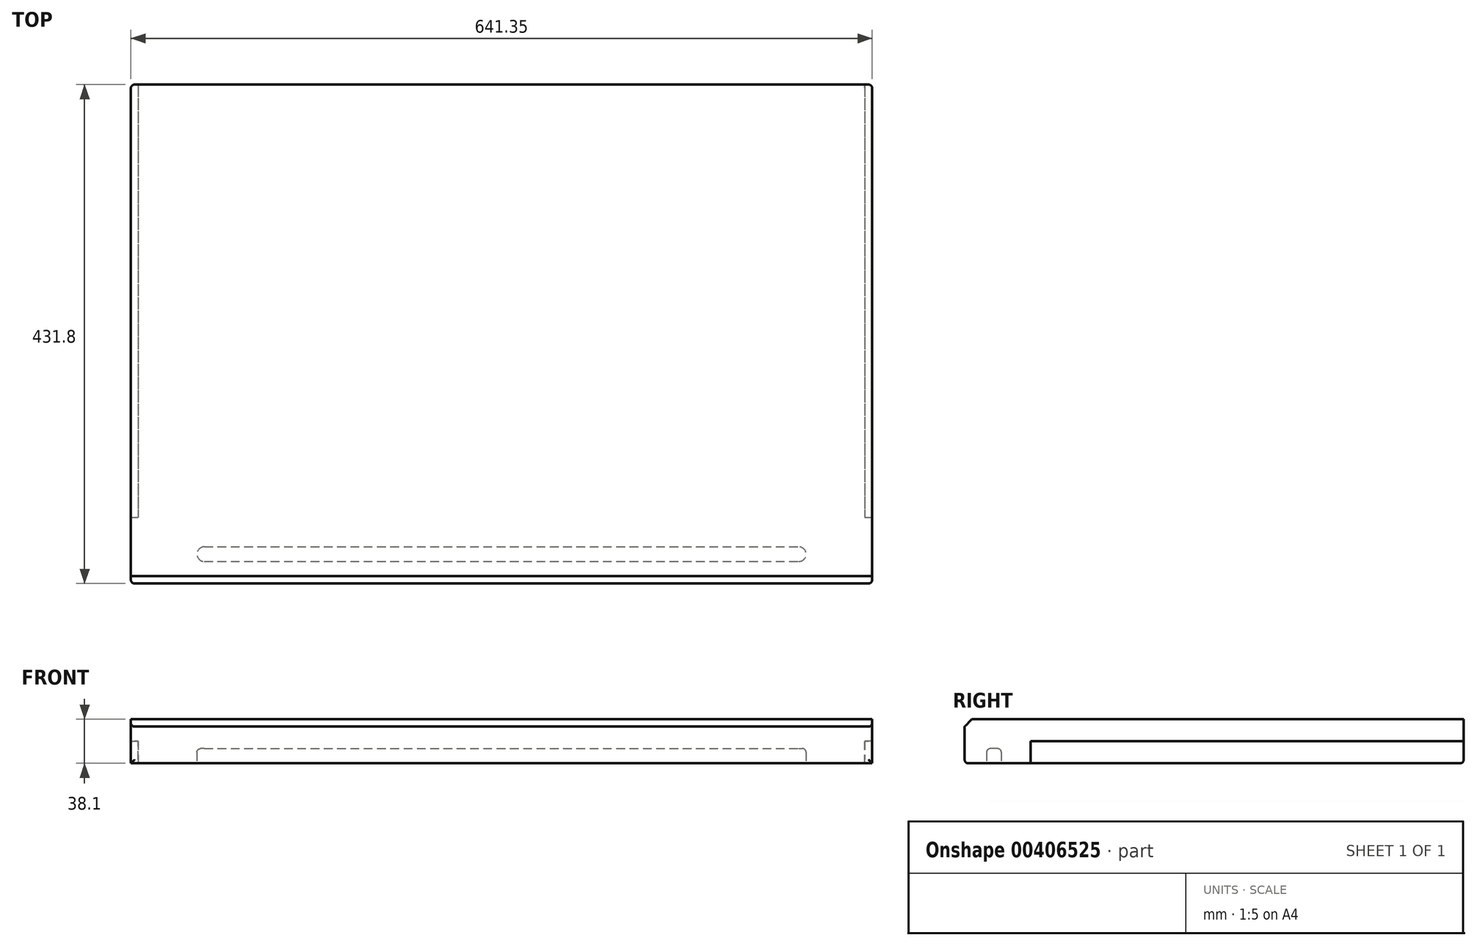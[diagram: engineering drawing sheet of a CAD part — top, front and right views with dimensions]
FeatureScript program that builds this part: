
annotation { "Feature Type Name" : "Feature", "Feature Type Description" : "" }
export const myFeature = defineFeature(function(context is Context, id is Id, definition is map)
    precondition{}
    {
        {
            var Q0;
            Q0=qCreatedBy(makeId("Top.planeOp"),FACE);
            var sketch = newSketch(context, id + "F0", { "sketchPlane" : qUnion([Q0])});
            skLineSegment(sketch, "E0.bottom", {"start": v(0, 0) * mm, "end": v(641.35, 0) * mm});
            skLineSegment(sketch, "E0.top", {"start": v(0, 431.8) * mm, "end": v(641.35, 431.8) * mm});
            skLineSegment(sketch, "E0.left", {"start": v(0, 0) * mm, "end": v(0, 431.8) * mm});
            skLineSegment(sketch, "E0.right", {"start": v(641.35, 0) * mm, "end": v(641.35, 431.8) * mm});
            skSolve(sketch);
        }
        {
            var Q0;
            Q0 = qSketchRegion(id + "F0", true);
            extrude(context, id + "F1", {"entities" : qUnion([Q0]), "depth" : 38.1 * mm});
        }
        {
            var Q0;
            Q0=makeQuery(id+"F1.opExtrude","SWEPT_FACE",FACE,{"disambiguationData":[OSD([sQuery(id+"F0.wireOp",EDGE,"E0.bottom")])]});
            var sketch = newSketch(context, id + "F2", { "sketchPlane" : qUnion([Q0])});
            skLineSegment(sketch, "E1.bottom", {"start": v(0, 19.05) * mm, "end": v(6.35, 19.05) * mm});
            skLineSegment(sketch, "E1.top", {"start": v(0, 0) * mm, "end": v(6.35, 0) * mm});
            skLineSegment(sketch, "E1.left", {"start": v(0, 19.05) * mm, "end": v(0, 0) * mm});
            skLineSegment(sketch, "E1.right", {"start": v(6.35, 19.05) * mm, "end": v(6.35, 0) * mm});
            skLineSegment(sketch, "E2.bottom", {"start": v(641.35, 0) * mm, "end": v(635, 0) * mm});
            skLineSegment(sketch, "E2.top", {"start": v(641.35, 19.05) * mm, "end": v(635, 19.05) * mm});
            skLineSegment(sketch, "E2.left", {"start": v(641.35, 0) * mm, "end": v(641.35, 19.05) * mm});
            skLineSegment(sketch, "E2.right", {"start": v(635, 0) * mm, "end": v(635, 19.05) * mm});
            skSolve(sketch);
        }
        {
            var Q0;
            Q0 = qSketchRegion(id + "F2", true);
            extrude(context, id + "F3", {"entities" : qUnion([Q0]), "operationType" : NewBodyOperationType.REMOVE, "endBound" : BoundingType.THROUGH_ALL, "oppositeDirection" : true, "depth" : 25.4 * mm});
        }
        {
            var Q0;
            Q0 = qSketchRegion(id + "F2", true);
            extrude(context, id + "F4", {"entities" : qUnion([Q0]), "operationType" : NewBodyOperationType.ADD, "oppositeDirection" : true, "depth" : 57.15 * mm});
        }
        {
            var Q0;
            Q0=makeQuery(id+"F1.opExtrude","CAP_EDGE",EDGE,{"disambiguationData":[OSD([sQuery(id+"F0.wireOp",EDGE,"E0.bottom")])],"isStart":false});
            var Q1;
            Q1=makeQuery(id+"F3r3F55hNGPta0S_1.opExtrude","CAP_EDGE",EDGE,{"disambiguationData":[OSD([sQuery(id+"FHEdhYLIMRPzULt_1.wireOp",EDGE,"pu4zk4sB-gXpi-S8tP-kPqK-HAcdQL3lesaA.top")])],"isStart":false});
            var Q2;
            Q2=makeQuery(id+"F3r3F55hNGPta0S_1.opExtrude","CAP_EDGE",EDGE,{"disambiguationData":[OSD([sQuery(id+"FHEdhYLIMRPzULt_1.wireOp",EDGE,"pu4zk4sB-gXpi-S8tP-kPqK-HAcdQL3lesaA.bottom")])],"isStart":false});
            chamfer(context, id + "F5", {"entities" : qUnion([Q0, Q1, Q2]), "width" : 6.35 * mm, "tangentPropagation" : true});
        }
        {
            var Q0;
            Q0=makeQuery(id+"F4.boolean.opBoolean","MERGE",FACE,{"derivedFrom":[makeQuery(id+"F1.opExtrude","CAP_FACE",FACE,{"disambiguationData":[OSD([sQuery(id+"F0.wireOp",EDGE,"E0.bottom"),sQuery(id+"F0.wireOp",EDGE,"E0.top"),sQuery(id+"F0.wireOp",EDGE,"E0.left"),sQuery(id+"F0.wireOp",EDGE,"E0.right")])],"isStart":true}),makeQuery(id+"F4.opExtrude","SWEPT_FACE",FACE,{"disambiguationData":[OSD([sQuery(id+"F2.wireOp",EDGE,"E1.top")])]}),makeQuery(id+"F4.opExtrude","SWEPT_FACE",FACE,{"disambiguationData":[OSD([sQuery(id+"F2.wireOp",EDGE,"E2.bottom")])]})]});
            var sketch = newSketch(context, id + "F6", { "sketchPlane" : qUnion([Q0])});
            skLineSegment(sketch, "E3.bottom", {"start": v(63.5, -19.05) * mm, "end": v(577.85, -19.05) * mm});
            skLineSegment(sketch, "E3.top", {"start": v(63.5, -31.75) * mm, "end": v(577.85, -31.75) * mm});
            skLineSegment(sketch, "E3.left", {"start": v(63.5, -19.05) * mm, "end": v(63.5, -31.75) * mm, "construction": true});
            skLineSegment(sketch, "E3.right", {"start": v(577.85, -19.05) * mm, "end": v(577.85, -31.75) * mm, "construction": true});
            skArc(sketch, "E4", {"start": v(63.5, -19.05) * mm, "mid": v(57.15, -25.4) * mm, "end": v(63.5, -31.75) * mm});
            skArc(sketch, "E5", {"start": v(577.85, -19.05) * mm, "mid": v(584.2, -25.4) * mm, "end": v(577.85, -31.75) * mm});
            skSolve(sketch);
        }
        {
            var Q0;
            Q0 = qSketchRegion(id + "F6", true);
            extrude(context, id + "F7", {"entities" : qUnion([Q0]), "operationType" : NewBodyOperationType.REMOVE, "oppositeDirection" : true, "depth" : 12.7 * mm});
        }
        {
            var Q0;
            Q0=makeQuery(id+"F1.opExtrude","SWEPT_EDGE",EDGE,{"disambiguationData":[OSD([sQuery(id+"F0.wireOp",EDGE,"E0.bottom"),sQuery(id+"F0.wireOp",EDGE,"E0.left")])]});
            var Q1;
            Q1=makeQuery(id+"F1.opExtrude","CAP_EDGE",EDGE,{"disambiguationData":[OSD([sQuery(id+"F0.wireOp",EDGE,"E0.bottom")])],"isStart":true});
            var Q2;
            Q2=makeQuery(id+"F1.opExtrude","SWEPT_EDGE",EDGE,{"disambiguationData":[OSD([sQuery(id+"F0.wireOp",EDGE,"E0.bottom"),sQuery(id+"F0.wireOp",EDGE,"E0.right")])]});
            var Q3;
            Q3=makeQuery(id+"F3r3F55hNGPta0S_1.boolean.opBoolean","MERGE",EDGE,{"derivedFrom":[makeQuery(id+"F1.opExtrude","SWEPT_EDGE",EDGE,{"disambiguationData":[OSD([sQuery(id+"F0.wireOp",EDGE,"E0.top"),sQuery(id+"F0.wireOp",EDGE,"E0.right")])]}),makeQuery(id+"F3r3F55hNGPta0S_1.opExtrude","SWEPT_EDGE",EDGE,{"disambiguationData":[OSD([sQuery(id+"FHEdhYLIMRPzULt_1.wireOp",EDGE,"pu4zk4sB-gXpi-S8tP-kPqK-HAcdQL3lesaA.bottom"),sQuery(id+"FHEdhYLIMRPzULt_1.wireOp",EDGE,"pu4zk4sB-gXpi-S8tP-kPqK-HAcdQL3lesaA.right")])]})]});
            var Q4;
            Q4=makeQuery(id+"F1.opExtrude","CAP_EDGE",EDGE,{"disambiguationData":[OSD([sQuery(id+"F0.wireOp",EDGE,"E0.top")])],"isStart":true});
            var Q5;
            Q5=makeQuery(id+"F3r3F55hNGPta0S_1.boolean.opBoolean","MERGE",EDGE,{"derivedFrom":[makeQuery(id+"F1.opExtrude","SWEPT_EDGE",EDGE,{"disambiguationData":[OSD([sQuery(id+"F0.wireOp",EDGE,"E0.top"),sQuery(id+"F0.wireOp",EDGE,"E0.left")])]}),makeQuery(id+"F3r3F55hNGPta0S_1.opExtrude","SWEPT_EDGE",EDGE,{"disambiguationData":[OSD([sQuery(id+"FHEdhYLIMRPzULt_1.wireOp",EDGE,"pu4zk4sB-gXpi-S8tP-kPqK-HAcdQL3lesaA.bottom"),sQuery(id+"FHEdhYLIMRPzULt_1.wireOp",EDGE,"pu4zk4sB-gXpi-S8tP-kPqK-HAcdQL3lesaA.left")])]})]});
            var Q6;
            Q6=makeQuery(id+"F3r3F55hNGPta0S_1.opExtrude","SWEPT_EDGE",EDGE,{"disambiguationData":[OSD([sQuery(id+"F0.wireOp",EDGE,"E0.left"),sQuery(id+"FHEdhYLIMRPzULt_1.wireOp",EDGE,"pu4zk4sB-gXpi-S8tP-kPqK-HAcdQL3lesaA.top"),sQuery(id+"FHEdhYLIMRPzULt_1.wireOp",EDGE,"pu4zk4sB-gXpi-S8tP-kPqK-HAcdQL3lesaA.left")])]});
            var Q7;
            Q7=makeQuery(id+"F3r3F55hNGPta0S_1.opExtrude","SWEPT_EDGE",EDGE,{"disambiguationData":[OSD([sQuery(id+"F0.wireOp",EDGE,"E0.right"),sQuery(id+"FHEdhYLIMRPzULt_1.wireOp",EDGE,"pu4zk4sB-gXpi-S8tP-kPqK-HAcdQL3lesaA.top"),sQuery(id+"FHEdhYLIMRPzULt_1.wireOp",EDGE,"pu4zk4sB-gXpi-S8tP-kPqK-HAcdQL3lesaA.right")])]});
            var Q8;
            Q8=makeQuery(id+"F7.boolean.opBoolean","COPY",EDGE,{"derivedFrom":makeQuery(id+"F7.opExtrude","CAP_EDGE",EDGE,{"disambiguationData":[OSD([sQuery(id+"F6.wireOp",EDGE,"E4")])],"isStart":true})});
            var Q9;
            Q9=makeQuery(id+"F7.boolean.opBoolean","COPY",EDGE,{"derivedFrom":makeQuery(id+"F7.opExtrude","CAP_EDGE",EDGE,{"disambiguationData":[OSD([sQuery(id+"F6.wireOp",EDGE,"E4")])],"isStart":false})});
            fillet(context, id + "F8", {"entities" : qUnion([Q0, Q1, Q2, Q3, Q4, Q5, Q6, Q7, Q8, Q9]), "radius" : 3.17 * mm, "tangentPropagation" : true, "allowEdgeOverflow" : false});
        }
    });
